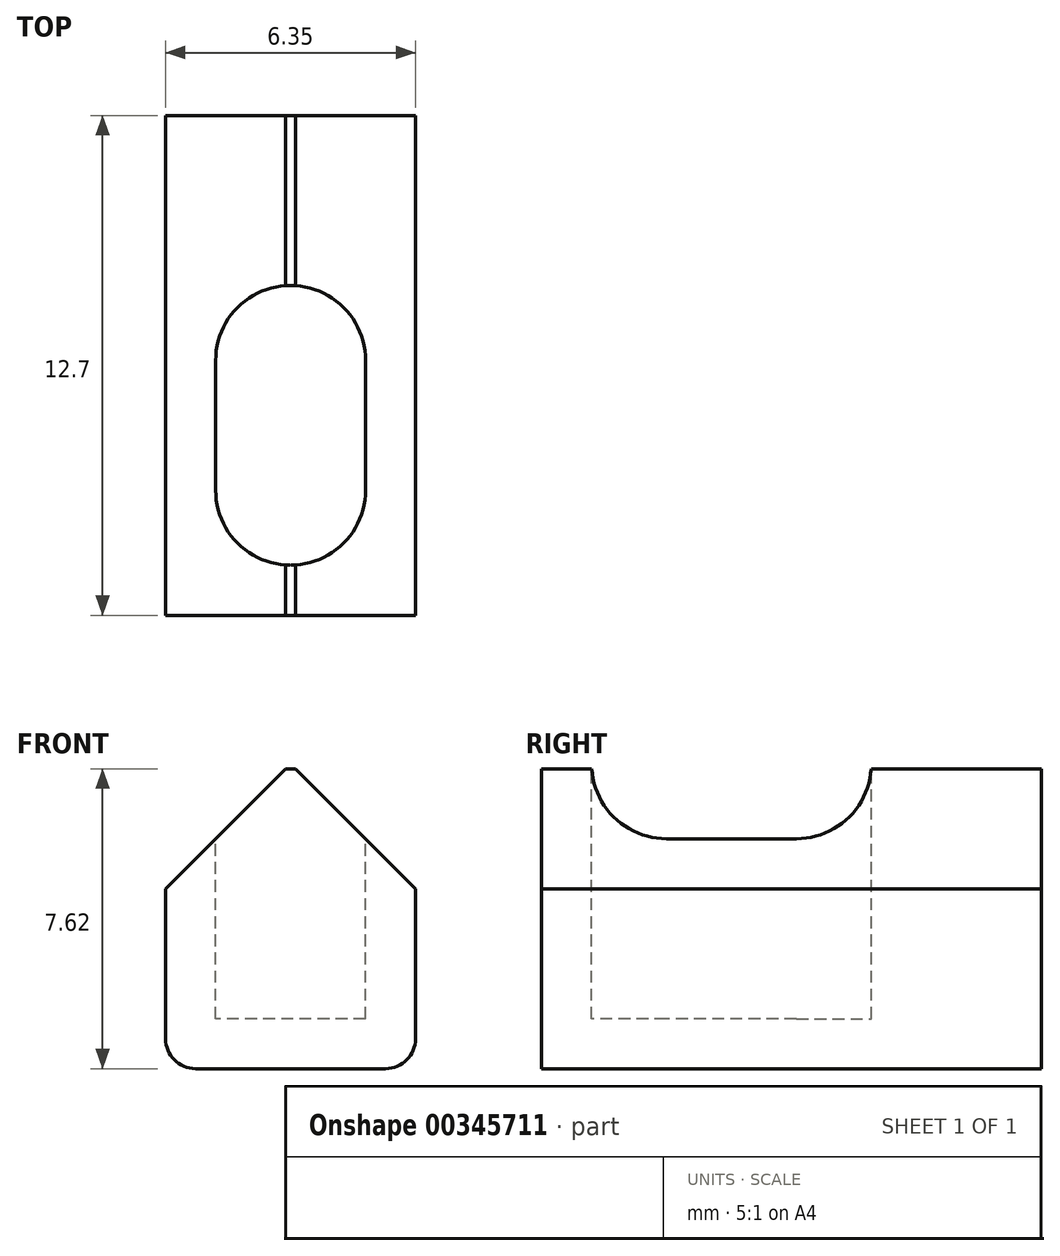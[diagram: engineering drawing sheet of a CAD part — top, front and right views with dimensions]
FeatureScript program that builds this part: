
annotation { "Feature Type Name" : "Feature", "Feature Type Description" : "" }
export const myFeature = defineFeature(function(context is Context, id is Id, definition is map)
    precondition{}
    {
        {
            var Q0;
            Q0=qCreatedBy(makeId("Top.planeOp"),FACE);
            var sketch = newSketch(context, id + "F0", { "sketchPlane" : qUnion([Q0])});
            skPoint(sketch, "E0.end.orphan", {"position": v(-50.8, 0) * mm});
            skLineSegment(sketch, "E1", {"start": v(-50.8, 0) * mm, "end": v(-50.8, -12.7) * mm});
            skLineSegment(sketch, "E2", {"start": v(-50.8, -12.7) * mm, "end": v(-44.45, -12.7) * mm});
            skLineSegment(sketch, "E3", {"start": v(-44.45, -12.7) * mm, "end": v(-44.45, 0) * mm});
            skLineSegment(sketch, "E4", {"start": v(-50.8, 0) * mm, "end": v(-44.45, 0) * mm});
            skSolve(sketch);
        }
        {
            var Q0;
            Q0=makeQuery(id+"F0.imprint","IMPRINT",FACE,{"disambiguationData":[TD([[makeQuery(id+"F0.imprint","IMPRINT",EDGE,{"derivedFrom":sQuery(id+"F0.wireOp",EDGE,"28nhrrkq-ehvW-D8SR-RhxH-8yo7QUcfZ6Or")}),1.0]])]});
            var Q1;
            Q1=makeQuery(id+"F0.imprint","IMPRINT",FACE,{"disambiguationData":[TD([[makeQuery(id+"F0.imprint","IMPRINT",EDGE,{"derivedFrom":sQuery(id+"F0.wireOp",EDGE,"E1")}),1.0]])]});
            extrude(context, id + "F1", {"entities" : qUnion([Q0, Q1]), "depth" : 7.62 * mm});
        }
        {
            var Q0;
            Q0=makeQuery(id+"F1.opExtrude","CAP_FACE",FACE,{"disambiguationData":[OSD([sQuery(id+"F0.wireOp",EDGE,"28nhrrkq-ehvW-D8SR-RhxH-8yo7QUcfZ6Or"),sQuery(id+"F0.wireOp",EDGE,"E1"),sQuery(id+"F0.wireOp",EDGE,"E2"),sQuery(id+"F0.wireOp",EDGE,"E3"),sQuery(id+"F0.wireOp",EDGE,"n7PWZTU9-4q6C-JVE9-l9ot-aJgFO7hGoHRH"),sQuery(id+"F0.wireOp",EDGE,"NfhRGeWc-Q845-1dfo-Wt4a-3j7KXOILvNuS"),sQuery(id+"F0.wireOp",EDGE,"ntAli3kE-xY2e-bvQE-zb23-rqoQVq3xnYWY"),sQuery(id+"F0.wireOp",EDGE,"HQ9O0PJx-BFkP-VK1U-Kdk3-RqgboQ3zqpkN"),sQuery(id+"F0.wireOp",EDGE,"LE1lmWo3-6Bj4-NADi-ik4c-iWQ5d6hpDMwv"),sQuery(id+"F0.wireOp",EDGE,"8XrB1TRp-GgfZ-jHfe-kxnx-fmZv9Wix6tOY"),sQuery(id+"F0.wireOp",EDGE,"O2qAttx2-6x4N-ts07-3464-9Wz6WEI1xALX"),sQuery(id+"F0.wireOp",EDGE,"DJJCWIbL-BvAU-0pEq-EVaK-LaSX72R2ZHMv"),sQuery(id+"F0.wireOp",EDGE,"jjuRchzx-SQkY-UAtB-fzIs-hsxS4BH9XNex"),sQuery(id+"F0.wireOp",EDGE,"hSZXNKDe-QdlA-Ubii-jfKe-uzTRfW14TiC6"),sQuery(id+"F0.wireOp",EDGE,"M8TUd0sq-VQoA-REuM-TEQ4-saRRINsm9XA6"),sQuery(id+"F0.wireOp",EDGE,"rzIIFNt3-eSPg-6uAS-bRmE-PIViqIlfKdIT"),sQuery(id+"F0.wireOp",EDGE,"BDyse0eD-Ba27-gQXA-DOoW-MKXNJAFasQbe"),sQuery(id+"F0.wireOp",EDGE,"kfjUxnD2-5uy3-9zBA-OiLM-U9Fx5LN0PdMd"),sQuery(id+"F0.wireOp",EDGE,"nsUrUylu-JKWz-Q0C5-Kwmc-zKBODmauxEv1"),sQuery(id+"F0.wireOp",EDGE,"hPeKGlVj-yzxi-P7Fg-A53b-50cN19y4VmkM")])],"isStart":false});
            var sketch = newSketch(context, id + "F2", { "sketchPlane" : qUnion([Q0])});
            skLineSegment(sketch, "E5", {"start": v(-49.53, -6.22) * mm, "end": v(-49.53, -9.53) * mm});
            skArc(sketch, "E6", {"start": v(-49.53, -9.53) * mm, "mid": v(-47.63, -11.43) * mm, "end": v(-45.72, -9.53) * mm});
            skLineSegment(sketch, "E7", {"start": v(-45.72, -9.53) * mm, "end": v(-45.72, -6.22) * mm});
            skArc(sketch, "E8", {"start": v(-49.53, -6.22) * mm, "mid": v(-47.63, -4.32) * mm, "end": v(-45.72, -6.22) * mm});
            skSolve(sketch);
        }
        {
            var Q0;
            Q0=makeQuery(id+"F2.imprint","IMPRINT",FACE,{"disambiguationData":[TD([[makeQuery(id+"F2.imprint","IMPRINT",EDGE,{"derivedFrom":sQuery(id+"F2.wireOp",EDGE,"4d2956ef-5765-4483-b3db-40ab5b381953")}),1.0]])]});
            var Q1;
            Q1=makeQuery(id+"F2.imprint","IMPRINT",FACE,{"disambiguationData":[TD([[makeQuery(id+"F2.imprint","IMPRINT",EDGE,{"derivedFrom":sQuery(id+"F2.wireOp",EDGE,"28797bc1-5a1d-426f-a72c-c29a9c017de3")}),1.0]])]});
            var Q2;
            Q2=makeQuery(id+"F2.imprint","IMPRINT",FACE,{"disambiguationData":[TD([[makeQuery(id+"F2.imprint","IMPRINT",EDGE,{"derivedFrom":sQuery(id+"F2.wireOp",EDGE,"17d464c9-c2ce-4821-9ec0-c2b6676a8ab8")}),1.0]])]});
            var Q3;
            Q3=makeQuery(id+"F2.imprint","IMPRINT",FACE,{"disambiguationData":[TD([[makeQuery(id+"F2.imprint","IMPRINT",EDGE,{"derivedFrom":sQuery(id+"F2.wireOp",EDGE,"9a2753a3-d09b-43fa-a831-6e5817566245")}),1.0]])]});
            var Q4;
            Q4=makeQuery(id+"F2.imprint","IMPRINT",FACE,{"disambiguationData":[TD([[makeQuery(id+"F2.imprint","IMPRINT",EDGE,{"derivedFrom":sQuery(id+"F2.wireOp",EDGE,"E5")}),1.0]])]});
            extrude(context, id + "F3", {"entities" : qUnion([Q0, Q1, Q2, Q3, Q4]), "operationType" : NewBodyOperationType.REMOVE, "oppositeDirection" : true, "depth" : 6.35 * mm});
        }
        {
            var Q0;
            Q0=makeQuery(id+"F1.opExtrude","CAP_EDGE",EDGE,{"disambiguationData":[OSD([sQuery(id+"F0.wireOp",EDGE,"E1")])],"isStart":false});
            var Q1;
            Q1=makeQuery(id+"F1.opExtrude","CAP_EDGE",EDGE,{"disambiguationData":[OSD([sQuery(id+"F0.wireOp",EDGE,"E3")])],"isStart":false});
            var Q2;
            Q2=makeQuery(id+"F1.opExtrude","CAP_EDGE",EDGE,{"disambiguationData":[OSD([sQuery(id+"F0.wireOp",EDGE,"NfhRGeWc-Q845-1dfo-Wt4a-3j7KXOILvNuS")])],"isStart":false});
            var Q3;
            Q3=makeQuery(id+"F1.opExtrude","CAP_EDGE",EDGE,{"disambiguationData":[OSD([sQuery(id+"F0.wireOp",EDGE,"HQ9O0PJx-BFkP-VK1U-Kdk3-RqgboQ3zqpkN")])],"isStart":false});
            var Q4;
            Q4=makeQuery(id+"F1.opExtrude","CAP_EDGE",EDGE,{"disambiguationData":[OSD([sQuery(id+"F0.wireOp",EDGE,"8XrB1TRp-GgfZ-jHfe-kxnx-fmZv9Wix6tOY")])],"isStart":false});
            var Q5;
            Q5=makeQuery(id+"F1.opExtrude","CAP_EDGE",EDGE,{"disambiguationData":[OSD([sQuery(id+"F0.wireOp",EDGE,"DJJCWIbL-BvAU-0pEq-EVaK-LaSX72R2ZHMv")])],"isStart":false});
            var Q6;
            Q6=makeQuery(id+"F1.opExtrude","CAP_EDGE",EDGE,{"disambiguationData":[OSD([sQuery(id+"F0.wireOp",EDGE,"hSZXNKDe-QdlA-Ubii-jfKe-uzTRfW14TiC6")])],"isStart":false});
            var Q7;
            Q7=makeQuery(id+"F1.opExtrude","CAP_EDGE",EDGE,{"disambiguationData":[OSD([sQuery(id+"F0.wireOp",EDGE,"rzIIFNt3-eSPg-6uAS-bRmE-PIViqIlfKdIT")])],"isStart":false});
            var Q8;
            Q8=makeQuery(id+"F1.opExtrude","CAP_EDGE",EDGE,{"disambiguationData":[OSD([sQuery(id+"F0.wireOp",EDGE,"kfjUxnD2-5uy3-9zBA-OiLM-U9Fx5LN0PdMd")])],"isStart":false});
            chamfer(context, id + "F4", {"entities" : qUnion([Q0, Q1, Q2, Q3, Q4, Q5, Q6, Q7, Q8]), "width" : 3.05 * mm, "tangentPropagation" : true});
        }
        {
            var Q0;
            Q0=makeQuery(id+"F1.opExtrude","CAP_EDGE",EDGE,{"disambiguationData":[OSD([sQuery(id+"F0.wireOp",EDGE,"E1")])],"isStart":true});
            var Q1;
            Q1=makeQuery(id+"F1.opExtrude","CAP_EDGE",EDGE,{"disambiguationData":[OSD([sQuery(id+"F0.wireOp",EDGE,"E3")])],"isStart":true});
            var Q2;
            Q2=makeQuery(id+"F1.opExtrude","CAP_EDGE",EDGE,{"disambiguationData":[OSD([sQuery(id+"F0.wireOp",EDGE,"n7PWZTU9-4q6C-JVE9-l9ot-aJgFO7hGoHRH")])],"isStart":true});
            var Q3;
            Q3=makeQuery(id+"F1.opExtrude","CAP_EDGE",EDGE,{"disambiguationData":[OSD([sQuery(id+"F0.wireOp",EDGE,"NfhRGeWc-Q845-1dfo-Wt4a-3j7KXOILvNuS")])],"isStart":true});
            var Q4;
            Q4=makeQuery(id+"F1.opExtrude","CAP_EDGE",EDGE,{"disambiguationData":[OSD([sQuery(id+"F0.wireOp",EDGE,"HQ9O0PJx-BFkP-VK1U-Kdk3-RqgboQ3zqpkN")])],"isStart":true});
            var Q5;
            Q5=makeQuery(id+"F1.opExtrude","CAP_EDGE",EDGE,{"disambiguationData":[OSD([sQuery(id+"F0.wireOp",EDGE,"ntAli3kE-xY2e-bvQE-zb23-rqoQVq3xnYWY")])],"isStart":true});
            var Q6;
            Q6=makeQuery(id+"F1.opExtrude","CAP_EDGE",EDGE,{"disambiguationData":[OSD([sQuery(id+"F0.wireOp",EDGE,"LE1lmWo3-6Bj4-NADi-ik4c-iWQ5d6hpDMwv")])],"isStart":true});
            var Q7;
            Q7=makeQuery(id+"F1.opExtrude","CAP_EDGE",EDGE,{"disambiguationData":[OSD([sQuery(id+"F0.wireOp",EDGE,"8XrB1TRp-GgfZ-jHfe-kxnx-fmZv9Wix6tOY")])],"isStart":true});
            var Q8;
            Q8=makeQuery(id+"F1.opExtrude","CAP_EDGE",EDGE,{"disambiguationData":[OSD([sQuery(id+"F0.wireOp",EDGE,"O2qAttx2-6x4N-ts07-3464-9Wz6WEI1xALX")])],"isStart":true});
            var Q9;
            Q9=makeQuery(id+"F1.opExtrude","CAP_EDGE",EDGE,{"disambiguationData":[OSD([sQuery(id+"F0.wireOp",EDGE,"DJJCWIbL-BvAU-0pEq-EVaK-LaSX72R2ZHMv")])],"isStart":true});
            var Q10;
            Q10=makeQuery(id+"F1.opExtrude","CAP_EDGE",EDGE,{"disambiguationData":[OSD([sQuery(id+"F0.wireOp",EDGE,"jjuRchzx-SQkY-UAtB-fzIs-hsxS4BH9XNex")])],"isStart":true});
            var Q11;
            Q11=makeQuery(id+"F1.opExtrude","CAP_EDGE",EDGE,{"disambiguationData":[OSD([sQuery(id+"F0.wireOp",EDGE,"hSZXNKDe-QdlA-Ubii-jfKe-uzTRfW14TiC6")])],"isStart":true});
            var Q12;
            Q12=makeQuery(id+"F1.opExtrude","CAP_EDGE",EDGE,{"disambiguationData":[OSD([sQuery(id+"F0.wireOp",EDGE,"M8TUd0sq-VQoA-REuM-TEQ4-saRRINsm9XA6")])],"isStart":true});
            var Q13;
            Q13=makeQuery(id+"F1.opExtrude","CAP_EDGE",EDGE,{"disambiguationData":[OSD([sQuery(id+"F0.wireOp",EDGE,"rzIIFNt3-eSPg-6uAS-bRmE-PIViqIlfKdIT")])],"isStart":true});
            var Q14;
            Q14=makeQuery(id+"F1.opExtrude","CAP_EDGE",EDGE,{"disambiguationData":[OSD([sQuery(id+"F0.wireOp",EDGE,"BDyse0eD-Ba27-gQXA-DOoW-MKXNJAFasQbe")])],"isStart":true});
            var Q15;
            Q15=makeQuery(id+"F1.opExtrude","CAP_EDGE",EDGE,{"disambiguationData":[OSD([sQuery(id+"F0.wireOp",EDGE,"kfjUxnD2-5uy3-9zBA-OiLM-U9Fx5LN0PdMd")])],"isStart":true});
            var Q16;
            Q16=makeQuery(id+"F1.opExtrude","CAP_EDGE",EDGE,{"disambiguationData":[OSD([sQuery(id+"F0.wireOp",EDGE,"nsUrUylu-JKWz-Q0C5-Kwmc-zKBODmauxEv1")])],"isStart":true});
            fillet(context, id + "F5", {"entities" : qUnion([Q0, Q1, Q2, Q3, Q4, Q5, Q6, Q7, Q8, Q9, Q10, Q11, Q12, Q13, Q14, Q15, Q16]), "radius" : 0.76 * mm, "tangentPropagation" : true, "allowEdgeOverflow" : false});
        }
    });
